# Revit family: Luxstatls
name_source: partatom
category: Communication Devices
revit_build: Autodesk Revit 2014 (Build: 20130308_1515(x64)
units: mm (PartAtom-declared; Revit-internal decimal feet)

## types (1)
- Luxstatls
    Assembly Code = D5090
    Certification = UL and cUL listed
    Default Elevation = 48 "
    Description = The Luxstat Light Sensor by Servodan provides the necessary daylight-level
information to the Luxstat daylight harvesting control modules. Using a
photodiode element, this sensor continuously measures daylight levels and
sends the information to the selected Luxstat daylight harvesting control
module.
    Features = Daylight sensor for Luxstat Daylight Harvesting System
• Architecturally attractive design
• Indoor and outdoor versions
• Open loop operation
• Foot-candle range: 3-6,000 fc
• Mounts vertically or horizontally
• Color coded, plug-and-play installation
• UL and cUL listed
• California Title 24 Compliant
    Housing Material = Glass - Hubbell - White
    Manufacturer = Hubbell Control Solutions
    Model = Luxstat Light Sensor
    Product Documentation Link = https://hubbellcdn.com
    Product Page URL = https://www.hubbell.com
    Sensing Element = Plastic - Hubbell - Gray
    Type Comments = Luxstat Light Sensor
    URL = https://www.hubbell.com
    Warranty = 5-Years Warranty
    Width = 2 "

## geometry (parser evidence)
native form markers: Sweep x1
no freeform markers — native parametric forms only
